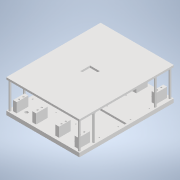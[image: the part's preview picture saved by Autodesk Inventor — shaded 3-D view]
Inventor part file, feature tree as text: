
AUTODESK INVENTOR PART (.ipt)
format: ipt  version: 2021 (Build 250183000, 183)  size: 486,400 bytes
history: native  units: mm
features: reference x19, other x15, extrude x10, sketch x10, projected_geometry x7, pattern_linear x3, loft x3, plane x2, fillet x2
ambient origin geometry x8: Origin, YZ Plane, XZ Plane, XY Plane, X Axis, Y Axis, Z Axis, Center Point
bodies: Solid1 (feature_tree)
feature tree (71):
  extrude  "Extrusion1"  Depth=130.0mm
  sketch  "Sketch2"  dims[d0=130.0mm d1=200.0mm]
  plane  "Work Plane1"
  extrude  "Extrusion2"  Depth=20.0mm
  pattern_linear  "Rectangular Pattern1"  Count1=2  [1 undecoded]
  extrude  "Extrusion4"  Depth=245.0mm
  extrude  "Extrusion5"  Depth=50.0mm
  extrude  "Extrusion6"  Depth=145.0mm
  sketch  "Sketch7"  dims[d16=90.0deg d17=145.0mm]
  pattern_linear  "Rectangular Pattern4"  Count1=2  [1 undecoded]
  pattern_linear  "Rectangular Pattern5"  Count1=6  [1 undecoded]
  extrude  "Extrusion9"  Depth=25.0mm TaperAngle=0.0deg
  extrude  "Extrusion10"  Depth=10.0mm
  extrude  "Extrusion11"  Depth=15.0mm TaperAngle=0.0deg
  plane  "Work Plane3"
  extrude  "Extrusion12"  TaperAngle=0.0deg  [1 undecoded]
  extrude  "Extrusion13"  Depth=25.0mm
  loft  "Loft1"
  loft  "Loft2"
  loft  "Loft3"
  fillet  "Fillet2"  Radius=20.0mm
  fillet  "Fillet3"  Radius=5.0mm
  reference  "Reference1"
  reference  "Reference2"
  reference  "Reference3"
  reference  "Reference4"
  reference  "Reference5"
  reference  "Reference6"
  reference  "Reference7"
  sketch  "Sketch4"  dims[d2=40.0mm d3=20.0mm d4=20.0mm d6=200.0mm d7=20.0mm d9=130.0mm]
  reference  "Reference13"
  reference  "Reference14"
  reference  "Reference15"
  reference  "Reference16"
  sketch  "Sketch5"  dims[d12=190.0mm d13=245.0mm]
  reference  "Reference17"
  reference  "Reference18"
  reference  "Reference19"
  reference  "Reference20"
  reference  "Reference21"
  reference  "Reference22"
  reference  "Reference23"
  reference  "Reference24"
  sketch  "Sketch6"  dims[d14=50.0mm d15=50.0mm]
  sketch  "Sketch10"  dims[d18=90.0deg]
  projected_geometry  "Projected Loop1"
  sketch  "Sketch11"  dims[d19=8.0mm d20=20.0mm d22=200.0mm d23=20.0mm d25=130.0mm]
  sketch  "Sketch12"  dims[d28=10.0mm d29=0.0mm d31=60.0mm]
  sketch  "Sketch13"  dims[d32=30.0mm d33=25.0mm d34=0.0mm]
  projected_geometry  "Projected Loop2"
  projected_geometry  "Projected Loop3"
  projected_geometry  "Projected Loop4"
  projected_geometry  "Projected Loop5"
  projected_geometry  "Projected Loop6"
  projected_geometry  "Projected Loop7"
  sketch  "Sketch14"  dims[d37=20.0mm d39=200.0mm d40=10.0mm d42=130.0mm d44=15.0mm d45=0.0mm d49=0.0mm d50=0.0mm d51=25.0mm d52=25.0mm d53=0.0mm d54=0.0mm d64=20.0mm d66=200.0mm d67=20.0mm d69=110.0mm d70=5.0mm d71=5.0mm d72=5.0mm d73=5.0mm d74=70.0mm d75=0.0mm d76=5.0mm d77=0.0mm d78=0.0mm d79=0.0mm d80=5.0mm d81=5.0mm d82=5.0mm d83=5.0mm d84=5.0mm d85=5.0mm d86=15.0mm d87=15.0mm d88=90.0mm d89=90.0mm d90=80.0mm d91=80.0mm d92=80.0mm d93=80.0mm d94=80.0mm d95=80.0mm d96=5.0mm d97=5.0mm d98=5.0mm d99=5.0mm d100=5.0mm d101=5.0mm d102=90.0mm d103=90.0mm d104=5.0mm d105=0.0mm d106=5.0mm d107=5.0mm d108=5.0mm d109=5.0mm d110=50.0mm d111=0.0mm d112=0.0mm d113=90.0deg d114=0.0mm d115=90.0deg d116=0.0mm d117=90.0deg d118=0.0mm d119=90.0deg d120=0.0mm d121=90.0deg d122=0.0mm d123=90.0deg d124=10.0mm d125=13.962634mm d126=10.0mm d35=0.5mm d36=0.872665mm d62=0.5mm d63=0.872665mm d65=0.872665mm]
  other  "Edges1"
  other  "Edges2"
  other  "Edges3"
  other  "Edges4"
  other  "Edges5"
  other  "Edges6"
  parser-record x1  (decoder bookkeeping rows leaked as tree rows — omitted from the tree; the rows remain in map.json)
  other  "ilmbt_3d_v1.iam"
  other  "MG-958 servo_MIR:1"
  other  "Part13_MIR:1"
  other  "MG-958 servo_MIR:2"
  other  "motor driver:1"
  other  "motor driver:4"
  other  "motor driver:3"
  other  "motor driver:2"
note: 4 required parameter values undecoded (feature->parameter linkage not recoverable at this tier; creation-order binding heuristic only, values carry confidence <= 0.55)
note: 1 file-system path scrubbed to <path> (originals preserved in map.json)
